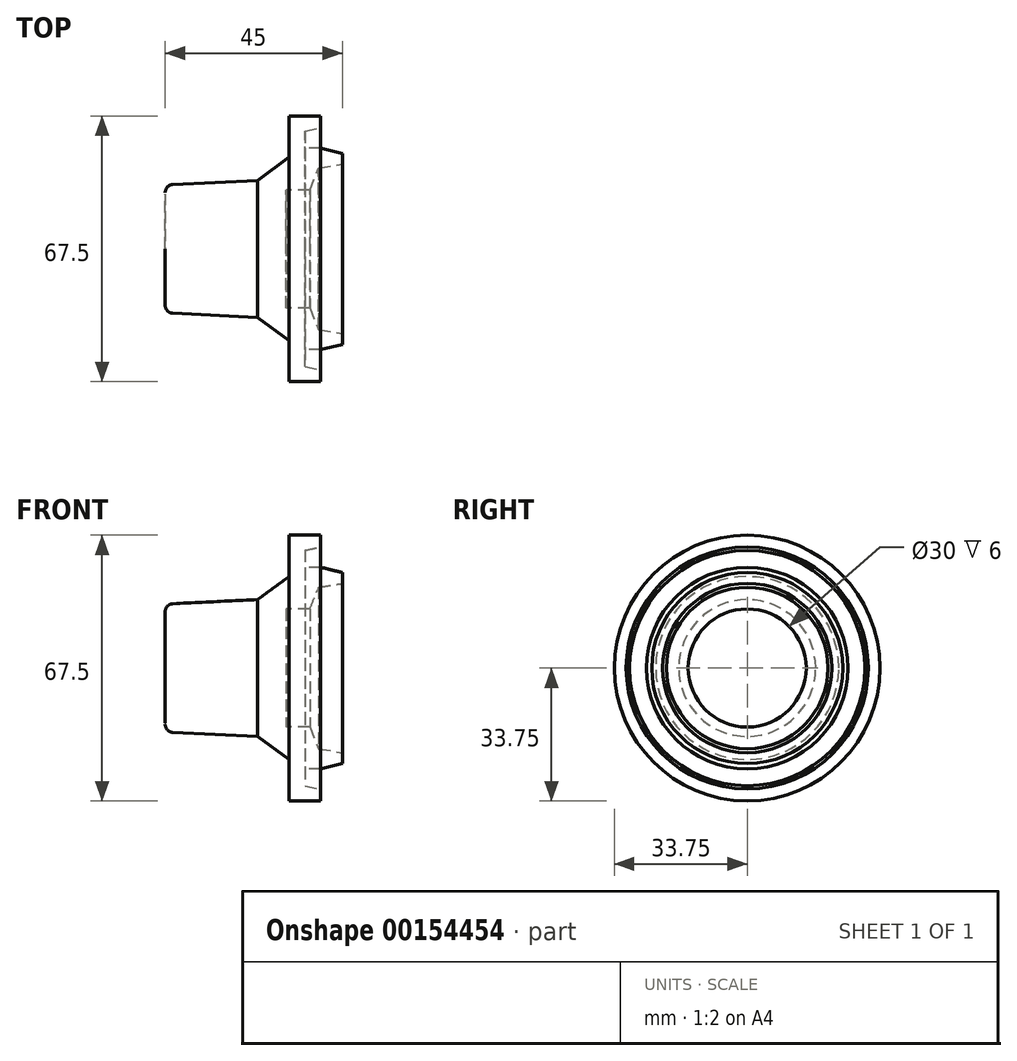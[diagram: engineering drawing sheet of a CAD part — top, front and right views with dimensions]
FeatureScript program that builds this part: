
annotation { "Feature Type Name" : "Feature", "Feature Type Description" : "" }
export const myFeature = defineFeature(function(context is Context, id is Id, definition is map)
    precondition{}
    {
        {
            var Q0;
            Q0=qCreatedBy(makeId("Front.planeOp"),FACE);
            var sketch = newSketch(context, id + "F0", { "sketchPlane" : qUnion([Q0])});
            skLineSegment(sketch, "E0", {"start": v(-28.83, -16.34) * mm, "end": v(-7.24, -17.4) * mm});
            skLineSegment(sketch, "E1", {"start": v(-7.24, -17.4) * mm, "end": v(0.76, -23.26) * mm});
            skLineSegment(sketch, "E2", {"start": v(0.76, -23.26) * mm, "end": v(0.76, -33.75) * mm});
            skLineSegment(sketch, "E3", {"start": v(0.76, -33.75) * mm, "end": v(8.76, -33.75) * mm});
            skLineSegment(sketch, "E4", {"start": v(8.76, -33.75) * mm, "end": v(8.76, -30.75) * mm});
            skLineSegment(sketch, "E5", {"start": v(8.76, -30.75) * mm, "end": v(4.76, -29.9) * mm});
            skLineSegment(sketch, "E6", {"start": v(4.76, -29.9) * mm, "end": v(4.76, -25.6) * mm});
            skLineSegment(sketch, "E7", {"start": v(4.76, -25.6) * mm, "end": v(8.76, -25.6) * mm});
            skLineSegment(sketch, "E8", {"start": v(8.76, -25.6) * mm, "end": v(14.26, -24.25) * mm});
            skLineSegment(sketch, "E9", {"start": v(14.26, -24.25) * mm, "end": v(14.26, -21.5) * mm});
            skLineSegment(sketch, "E10", {"start": v(14.26, -21.5) * mm, "end": v(8.26, -20.5) * mm});
            skLineSegment(sketch, "E11", {"start": v(8.26, -20.5) * mm, "end": v(6, -15) * mm});
            skLineSegment(sketch, "E12", {"start": v(6, -15) * mm, "end": v(0, -15) * mm});
            skLineSegment(sketch, "E13", {"start": v(0, -15) * mm, "end": v(0, 0) * mm});
            skPoint(sketch, "E14", {"position": v(-30.74, 0) * mm});
            skLineSegment(sketch, "E15", {"start": v(-36.32, 0) * mm, "end": v(19.82, 0) * mm});
            skPoint(sketch, "E16.visualSharp", {"position": v(-30.74, -16.25) * mm});
            skArc(sketch, "E16.filletArc", {"start": v(-30.74, -14.35) * mm, "mid": v(-30.18, -15.72) * mm, "end": v(-28.83, -16.34) * mm});
            skLineSegment(sketch, "E17", {"start": v(-30.74, 0) * mm, "end": v(-30.74, -14.35) * mm});
            skSolve(sketch);
        }
        {
            var Q0;
            Q0=makeQuery(id+"F0.imprint","IMPRINT",FACE,{"disambiguationData":[TD([[makeQuery(id+"F0.imprint","IMPRINT",EDGE,{"derivedFrom":sQuery(id+"F0.wireOp",EDGE,"E0")}),1.0]])]});
            var Q1;
            Q1=sQuery(id+"F0.wireOp",EDGE,"E15");
            revolve(context, id + "F1", {"entities" : qUnion([Q0]), "axis" : qUnion([Q1]), "revolveType" : RevolveType.FULL});
        }
    });
